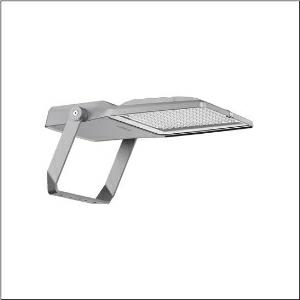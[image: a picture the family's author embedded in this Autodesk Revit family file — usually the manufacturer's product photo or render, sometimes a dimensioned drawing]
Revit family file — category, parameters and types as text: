
# Revit family: floodlight_fl_21_midi___pl43_5xa7786e4a1a_b497
name_source: partatom
category: Lighting Fixtures
units: mm (PartAtom-declared; Revit-internal decimal feet)

## family parameters
Cut with Voids When Loaded = No
Host = Face
Light Source = No
Part Type = Normal
Room Calculation Point = No
Round Connector Dimension = Use Diameter
Shared = No

## types (1)
- --- (1 x LED, 28830 lm, 212.4 W, 4000K)
    Apparent Load = 212 VA
    CIE Flux Codes = 27 78 99 100 100
    Color Rendering = 70
    Color Temperature = 4000K
    Default Elevation = 1800 mm
    Description = Floodlight FL 21 midi, floodlight, primary light control with lens, of PMMA, primary optical cover: protective disc, of toughened safety glass, transparent, light distribution: PL43, light emission: direct distribution, installation type: surface-mounted, LED, High Power LED, rated luminous flux: 28.830lm, luminous efficacy: 136lm/W, light colour: 740, colour temperature: 4000K, control gear: Smart Interface (Zhaga)D4i, control: overheat protection, constant luminous flux control, time-dependent luminous flux control, flexible luminous flux parameterisation, pre-setting: logarithmic dimming characteristic, with terminal, 6-pole, mains connection: 220..240V, AC, 50/60Hz, start of lifetime: 212W, end of service life: 231W, reduction: 95W, mounting bracket, of diecast aluminium, powder-coated, Siteco® metallic grey (DB 702S), corrosivity category C5 mid according to DIN EN ISO 12944, suitable for swimming pools, chlorine-resistant, sealing non-destructively replaceable, mounting bracket, of steel, galvanised, powder-coated, Siteco® metallic grey (DB 702S), Smart Interface below and above, protection rating (complete): IP66, insulation class (complete): insulation class II (safety insulation), certification: CE, ENEC, VDE, protection symbol: D, impact resistance: IK08, permissible operating ambient temperature: -40..+40°C, permissible operating ambient temperature for outdoor applications: -40..+50°C, standard: DIN EN 12944, LABS conformity tested according to VDMA 24364:2018-05, packaging unit: 1 piece

Light Distribution: PL43
    Height = 76 mm
    Lamp = 1 x LED
    Lamp Light Flux = 28830 lm
    Lamp Power = 212.4 W
    Lamp count = 1
    Length = 657 mm
    Luminous efficacy = 136 lm/W
    Manufacturer = Siteco
    ModVariant = No
    Model = 5XA7786E4A1A
    Number of Poles = 1
    OnlyDefault = Yes
    Power Factor = 1
    Product Name = Floodlight FL 21 midi | PL43
    Product group = floodlight | pylon annexe
    ProductGroupID = 6201
    Protection Class = Protection class II
    Protection Degree = IP 66
    RLX_Detail_Level = 1
    RLX_Emergency_Light_Flux = 0 lm
    RLX_Emergency_Type = 0
    RLX_Emergency_Type_DB = No
    RlxData = <blob elided: 101717 chars, md5=d379d98b>
    Socket = socket
    Standby Power = 0 W
    System Light Flux = 28830 lm
    System Power = 212 W
    Type Comments = factory setting: luminous flux: 100 % | dim-lin: 254 | 710 mA
    Type Image = l_1006876.jpg
    URL = http://relux.com
    VarID = @adj_110735
    Voltage = 0 V
    Weight = 0.00 kg
    Width = 442 mm

## geometry (parser evidence)
native form markers: Blend x4, Sweep x12
no freeform markers — native parametric forms only
